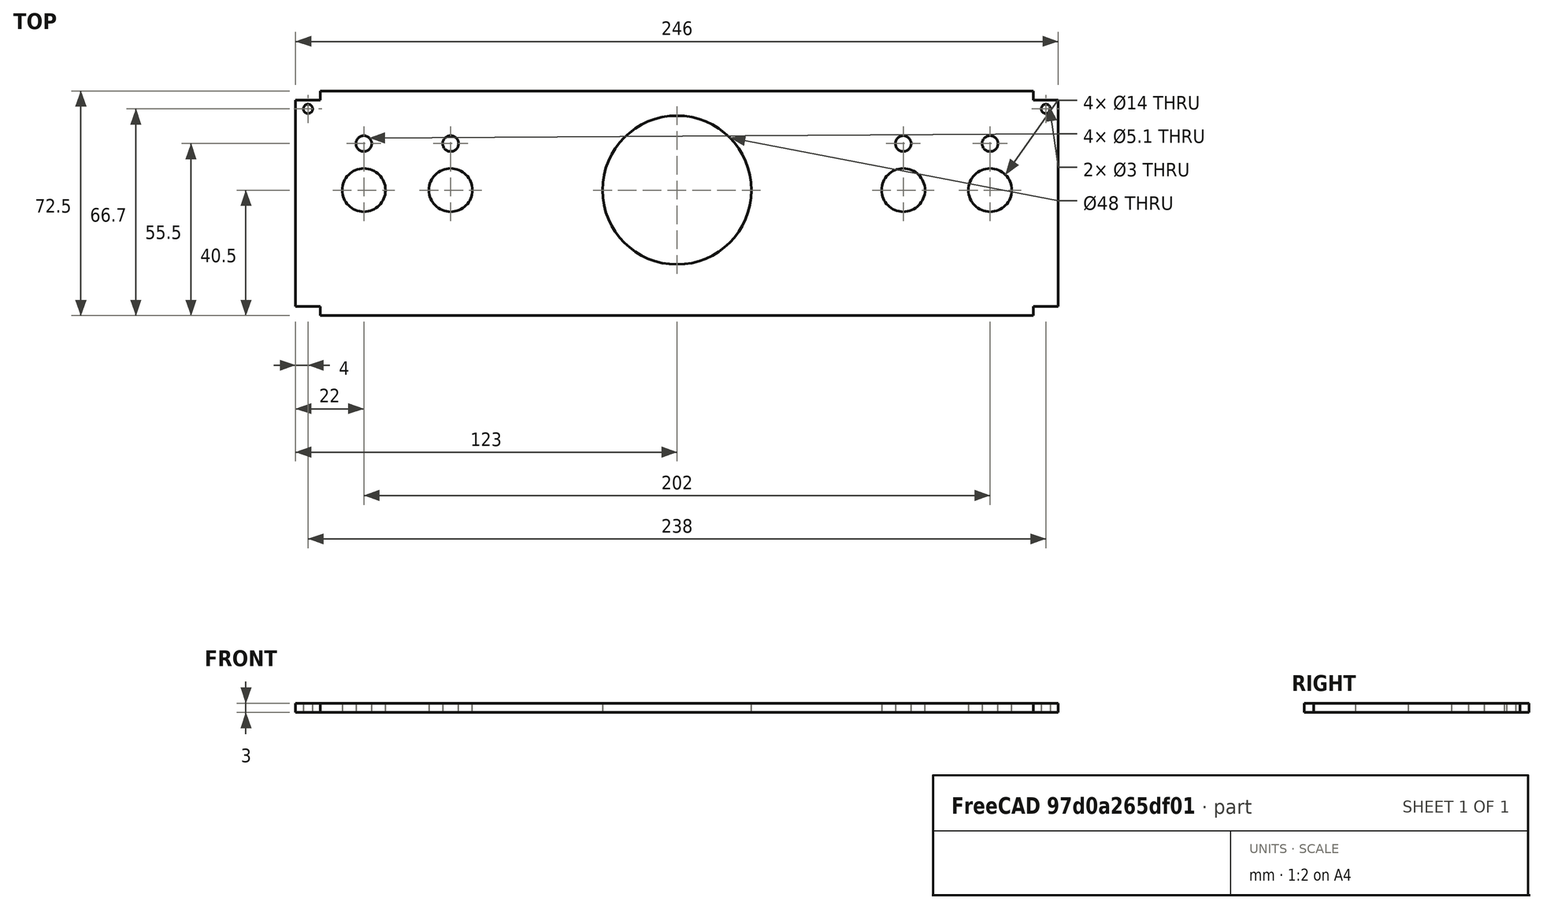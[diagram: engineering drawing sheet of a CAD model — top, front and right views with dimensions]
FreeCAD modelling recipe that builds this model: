
FCSTD DOCUMENT  (FreeCAD 0.19R24291 (Git))
Label: ri-buttoncover
License: All rights reserved
LicenseURL: http://en.wikipedia.org/wiki/All_rights_reserved
objects: Sketcher::SketchObject×2, PartDesign::Pad×1, PartDesign::Body×1, Part::Part2DObjectPython×1
note: 6 computed .brp shape members not serialized (recipe doc carries the construction recipe); baked Part::Feature solids carry a one-line shape summary decoded from their .brp

FEATURE [Sketcher::SketchObject] Sketch
  FullyConstrained = true
  MapMode = 5
  Support = -> [XY_Plane]
  expr: Constraints[69] = .Constraints.buttondistance
  sketch-geometry (34):
    g0: LineSegment StartX=-123 StartY=33.25 StartZ=0 EndX=-115 EndY=33.25 EndZ=0
    g1: LineSegment StartX=-115 StartY=33.25 StartZ=0 EndX=-115 EndY=36.25 EndZ=0
    g2: LineSegment StartX=-115 StartY=36.25 StartZ=0 EndX=115 EndY=36.25 EndZ=0
    g3: LineSegment StartX=115 StartY=36.25 StartZ=0 EndX=115 EndY=33.25 EndZ=0
    g4: LineSegment StartX=115 StartY=33.25 StartZ=0 EndX=123 EndY=33.25 EndZ=0
    g5: LineSegment StartX=123 StartY=33.25 StartZ=0 EndX=123 EndY=-33.25 EndZ=0
    g6: LineSegment StartX=123 StartY=-33.25 StartZ=0 EndX=115 EndY=-33.25 EndZ=0
    g7: LineSegment StartX=115 StartY=-33.25 StartZ=0 EndX=115 EndY=-36.25 EndZ=0
    g8: LineSegment StartX=115 StartY=-36.25 StartZ=0 EndX=-115 EndY=-36.25 EndZ=0
    g9: LineSegment StartX=-115 StartY=-36.25 StartZ=0 EndX=-115 EndY=-33.25 EndZ=0
    g10: LineSegment StartX=-115 StartY=-33.25 StartZ=0 EndX=-123 EndY=-33.25 EndZ=0
    g11: LineSegment StartX=-123 StartY=-33.25 StartZ=0 EndX=-123 EndY=33.25 EndZ=0
    g12: Circle CenterX=0 CenterY=4.25 CenterZ=0 NormalX=0 NormalY=0 NormalZ=1 AngleXU=0 Radius=24
    g13: LineSegment StartX=-123 StartY=4.25 StartZ=0 EndX=123 EndY=4.25 EndZ=0
    g14: Circle CenterX=-101 CenterY=4.25 CenterZ=0 NormalX=0 NormalY=0 NormalZ=1 AngleXU=0 Radius=7
    g15: Circle CenterX=-73 CenterY=4.25 CenterZ=0 NormalX=0 NormalY=0 NormalZ=1 AngleXU=0 Radius=7
    g16: Circle CenterX=73 CenterY=4.25 CenterZ=0 NormalX=0 NormalY=0 NormalZ=1 AngleXU=0 Radius=7
    g17: Circle CenterX=101 CenterY=4.25 CenterZ=0 NormalX=0 NormalY=0 NormalZ=1 AngleXU=0 Radius=7
    g18: GeomPoint X=-66 Y=4.25 Z=0
    g19: GeomPoint X=66 Y=4.25 Z=0
    g20: Circle CenterX=-101 CenterY=19.25 CenterZ=0 NormalX=0 NormalY=0 NormalZ=1 AngleXU=0 Radius=2.55
    g21: Circle CenterX=-73 CenterY=19.25 CenterZ=0 NormalX=0 NormalY=0 NormalZ=1 AngleXU=0 Radius=2.55
    g22: Circle CenterX=73 CenterY=19.25 CenterZ=0 NormalX=0 NormalY=0 NormalZ=1 AngleXU=0 Radius=2.55
    g23: Circle CenterX=101 CenterY=19.25 CenterZ=0 NormalX=0 NormalY=0 NormalZ=1 AngleXU=0 Radius=2.55
    g24: LineSegment StartX=-115 StartY=33.25 StartZ=0 EndX=-115 EndY=-33.25 EndZ=0
    g25: LineSegment StartX=-115 StartY=33.25 StartZ=0 EndX=115 EndY=33.25 EndZ=0
    g26: LineSegment StartX=115 StartY=33.25 StartZ=0 EndX=115 EndY=-33.25 EndZ=0
    g27: GeomPoint X=-115 Y=-24.75 Z=0
    g28: GeomPoint X=115 Y=-24.75 Z=0
    g29: LineSegment StartX=-115 StartY=-24.75 StartZ=0 EndX=115 EndY=-24.75 EndZ=0
    g30: Circle CenterX=-119 CenterY=30.45 CenterZ=0 NormalX=0 NormalY=0 NormalZ=1 AngleXU=0 Radius=1.5
    g31: Circle CenterX=119 CenterY=30.45 CenterZ=0 NormalX=0 NormalY=0 NormalZ=1 AngleXU=0 Radius=1.5
    g32: GeomPoint X=-119 Y=33.25 Z=0
    g33: GeomPoint X=119 Y=33.25 Z=0
  constraints (89):
    c: Horizontal(g0)
    c: Coincident(g0,g1)
    c: Vertical(g1)
    c: Coincident(g1,g2)
    c: Horizontal(g2)
    c: Coincident(g2,g3)
    c: Vertical(g3)
    c: Coincident(g3,g4)
    c: Horizontal(g4)
    c: Coincident(g4,g5)
    c: Vertical(g5)
    c: Coincident(g5,g6)
    c: Horizontal(g6)
    c: Coincident(g6,g7)
    c: Vertical(g7)
    c: Coincident(g7,g8)
    c: Horizontal(g8)
    c: Coincident(g8,g9)
    c: Vertical(g9)
    c: Coincident(g9,g10)
    c: Horizontal(g10)
    c: Coincident(g10,g11)
    c: Vertical(g11)
    c: Coincident(g0,g11)
    c: Equal(g9,g7)
    c: Equal(g7,g3)
    c: Equal(g3,g1)
    c: DistanceY(g1,g1) = 3
    c: Equal(g0,g4)
    c: Equal(g4,g6)
    c: DistanceX(g0,g0) = 8
    c: DistanceY(g8,g1) = 72.5
    c: DistanceX(g10,g5) = 246
    c: Equal(g10,g6)
    c: Symmetric(g6,g0,g-1)
    c: Diameter(g12) = 48
    c: DistanceY(g8,g12) = 40.5
    c: PointOnObject(g13,g11)
    c: PointOnObject(g13,g5)
    c: Horizontal(g13)
    c: PointOnObject(g12,g13)
    c: PointOnObject(g14,g13)
    c: PointOnObject(g15,g13)
    c: PointOnObject(g17,g13)
    c: PointOnObject(g16,g13)
    c: Equal(g14,g15)
    c: Equal(g15,g16)
    c: Equal(g16,g17)
    c: Diameter(g14) = 14
    c: PointOnObject(g18,g13)
    c: Symmetric(g19,g18,g12)
    c: PointOnObject(g12,g-2)
    c: DistanceX(g18,g19) = 132
    c: Equal(g23,g22)
    c: Equal(g22,g21)
    c: Equal(g21,g20)
    c: Diameter(g20) = 5.1
    c: Horizontal(g20,g21)
    c: Horizontal(g21,g22)
    c: Horizontal(g22,g23)
    c: Vertical(g14,g20)
    c: DistanceY(g14,g20) = 15
    c: Vertical(g21,g15)
    c: Vertical(g16,g22)
    c: Vertical(g17,g23)
    c: PointOnObject(g19,g16)
    c: PointOnObject(g18,g15)
    c: DistanceX(g14,g15) = 28  'buttondistance'
    c: Coincident(g24,g0)
    c: DistanceX(g16,g17) = 28
    c: Coincident(g25,g0)
    c: Coincident(g26,g3)
    c: PointOnObject(g27,g24)
    c: PointOnObject(g28,g26)
    c: DistanceY(g27,g12) = 29
    c: Horizontal(g28,g27)
    c: Coincident(g29,g27)
    c: Equal(g31,g30)
    c: Horizontal(g30,g31)
    c: Diameter(g30) = 3
    c: DistanceY(g30,g0) = 2.8
    c: Symmetric(g0,g0,g32)
    c: Vertical(g30,g32)
    c: Symmetric(g4,g3,g33)
    c: Vertical(g31,g33)
    c: Coincident(g29,g28)
    c: Coincident(g24,g9)
    c: Coincident(g26,g6)
    c: Coincident(g25,g3)
FEATURE [PartDesign::Pad] Pad
  Direction = (1,1,1)
  Length = 3
  Length2 = 100
  Profile = -> Sketch
  Refine = true
  Type = 0
FEATURE [PartDesign::Body] Body
  Group = -> [Sketch,Pad]
  Origin = -> Origin
  Tip = -> Pad
FEATURE [Part::Part2DObjectPython] Shape2DView  # Draft 2D object (typed FeaturePython)
  Base = -> Pad
  FaceNumbers = [24]
  FuseArch = false
  HiddenLines = false
  InPlace = true
  Projection = (0,0,1)
  ProjectionMode = 0
  SegmentLength = 0.05
  Tessellation = false
  VisibleOnly = false
FEATURE [Sketcher::SketchObject] Sketch001
  FullyConstrained = false
  sketch-geometry (23):
    g0: LineSegment StartX=-123 StartY=33.25 StartZ=0 EndX=-115 EndY=33.25 EndZ=0
    g1: LineSegment StartX=-115 StartY=33.25 StartZ=0 EndX=-115 EndY=36.25 EndZ=0
    g2: LineSegment StartX=-115 StartY=36.25 StartZ=0 EndX=115 EndY=36.25 EndZ=0
    g3: LineSegment StartX=115 StartY=36.25 StartZ=0 EndX=115 EndY=33.25 EndZ=0
    g4: LineSegment StartX=115 StartY=33.25 StartZ=0 EndX=123 EndY=33.25 EndZ=0
    g5: LineSegment StartX=123 StartY=33.25 StartZ=0 EndX=123 EndY=-33.25 EndZ=0
    g6: LineSegment StartX=123 StartY=-33.25 StartZ=0 EndX=115 EndY=-33.25 EndZ=0
    g7: LineSegment StartX=115 StartY=-33.25 StartZ=0 EndX=115 EndY=-36.25 EndZ=0
    g8: LineSegment StartX=115 StartY=-36.25 StartZ=0 EndX=-115 EndY=-36.25 EndZ=0
    g9: LineSegment StartX=-115 StartY=-36.25 StartZ=0 EndX=-115 EndY=-33.25 EndZ=0
    g10: LineSegment StartX=-115 StartY=-33.25 StartZ=0 EndX=-123 EndY=-33.25 EndZ=0
    g11: LineSegment StartX=-123 StartY=-33.25 StartZ=0 EndX=-123 EndY=33.25 EndZ=0
    g12: Circle CenterX=0 CenterY=4.25 CenterZ=0 NormalX=0 NormalY=0 NormalZ=1 AngleXU=0 Radius=24
    g13: Circle CenterX=73 CenterY=4.25 CenterZ=0 NormalX=0 NormalY=0 NormalZ=1 AngleXU=0 Radius=7
    g14: Circle CenterX=101 CenterY=4.25 CenterZ=0 NormalX=0 NormalY=0 NormalZ=1 AngleXU=0 Radius=7
    g15: Circle CenterX=-73 CenterY=4.25 CenterZ=0 NormalX=0 NormalY=0 NormalZ=1 AngleXU=0 Radius=7
    g16: Circle CenterX=-101 CenterY=4.25 CenterZ=0 NormalX=0 NormalY=0 NormalZ=1 AngleXU=0 Radius=7
    g17: Circle CenterX=73 CenterY=19.25 CenterZ=0 NormalX=0 NormalY=0 NormalZ=1 AngleXU=0 Radius=2.55
    g18: Circle CenterX=101 CenterY=19.25 CenterZ=0 NormalX=0 NormalY=0 NormalZ=1 AngleXU=0 Radius=2.55
    g19: Circle CenterX=-73 CenterY=19.25 CenterZ=0 NormalX=0 NormalY=0 NormalZ=1 AngleXU=0 Radius=2.55
    g20: Circle CenterX=-101 CenterY=19.25 CenterZ=0 NormalX=0 NormalY=0 NormalZ=1 AngleXU=0 Radius=2.55
    g21: Circle CenterX=-119 CenterY=30.45 CenterZ=0 NormalX=0 NormalY=0 NormalZ=1 AngleXU=0 Radius=1.5
    g22: Circle CenterX=119 CenterY=30.45 CenterZ=0 NormalX=0 NormalY=0 NormalZ=1 AngleXU=0 Radius=1.5
